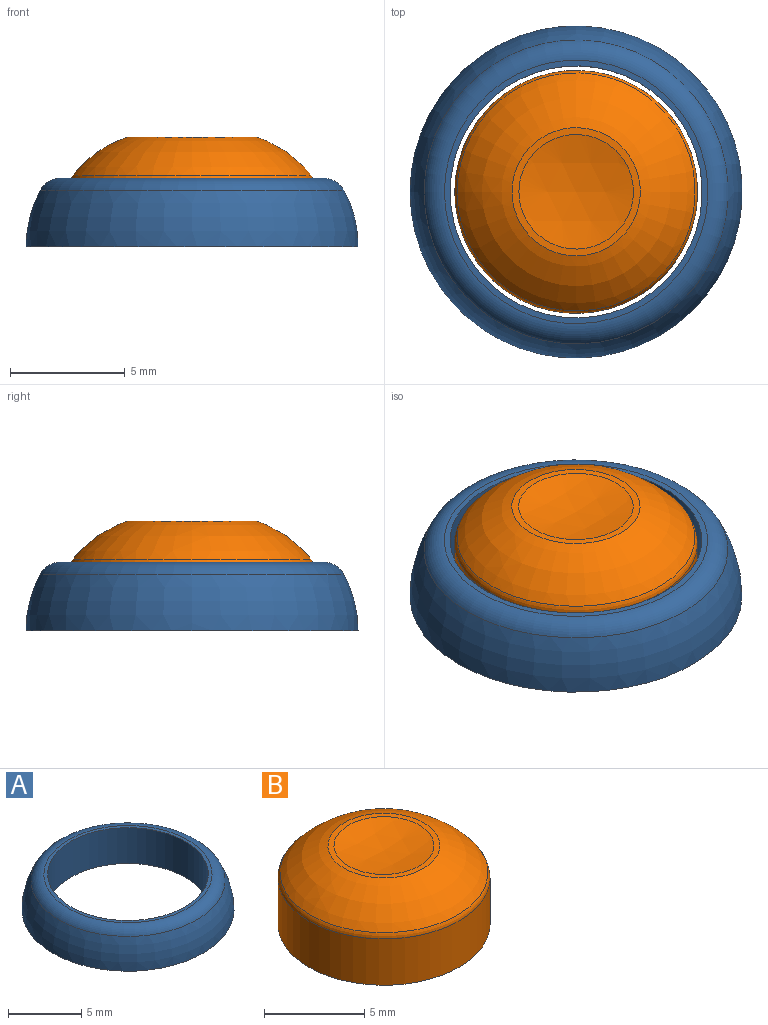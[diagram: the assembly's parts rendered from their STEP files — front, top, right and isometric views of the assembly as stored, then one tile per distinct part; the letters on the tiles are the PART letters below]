
ASSEMBLY  parts=2 mates=1
PART A: 5 faces, bbox 14.6x14.6x3 mm
  f0: cylinder r=5.5mm len=11mm, axis (0,0,-1), area 103.7mm2, adj f3,f4
  f1: torus R=5.75mm, axis (0,0,-1), area 42.4mm2, adj f2,f3
  f2: torus R=2mm, axis (0,0,-1), area 113.8mm2, adj f1,f4
  f3: plane 11.5x11.5mm, normal (0,0,1), area 8.8mm2, adj f0,f1
  f4: plane 14.5x14.5mm, normal (0,0,-1), area 70.1mm2, adj f0,f2
PART B: 6 faces, bbox 11.5x11.5x5.1 mm
  f0: sphere r=10.57mm, area 19.9mm2, adj f5
  f1: torus R=1.27mm, axis (0,0,-1), area 75.7mm2, adj f2,f5
  f2: torus R=4.8mm, axis (0,0,-1), area 11.1mm2, adj f1,f3
  f3: cylinder r=5.3mm len=10.6mm, axis (0,0,-1), area 94.3mm2, adj f2,f4
  f4: plane 10.6x10.6mm, normal (0,0,-1), area 88.2mm2, adj f3
  f5: plane 5.6x5.6mm, normal (0,0,1), area 5mm2, adj f0,f1
PLACE A at identity fixed
PLACE B at identity
MATE fastened A.f0 <-> B.f3  axis (0,0,-1) through (0,0,18)mm
